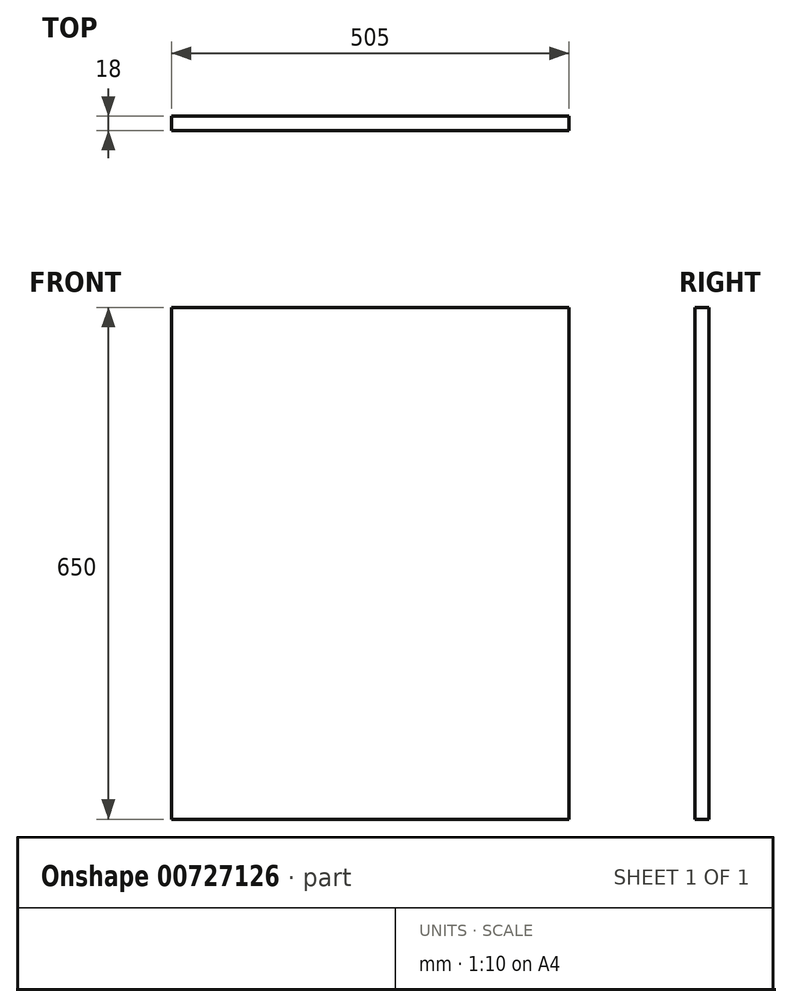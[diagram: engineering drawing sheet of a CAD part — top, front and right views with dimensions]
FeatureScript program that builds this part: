
annotation { "Feature Type Name" : "Feature", "Feature Type Description" : "" }
export const myFeature = defineFeature(function(context is Context, id is Id, definition is map)
    precondition{}
    {
        {
            var Q0;
            Q0=qCreatedBy(makeId("Front.planeOp"),FACE);
            var sketch = newSketch(context, id + "F0", { "sketchPlane" : qUnion([Q0])});
            skLineSegment(sketch, "E0.bottom", {"start": v(0, 0) * mm, "end": v(505, 0) * mm});
            skLineSegment(sketch, "E0.top", {"start": v(0, 650) * mm, "end": v(505, 650) * mm});
            skLineSegment(sketch, "E0.left", {"start": v(0, 0) * mm, "end": v(0, 650) * mm});
            skLineSegment(sketch, "E0.right", {"start": v(505, 0) * mm, "end": v(505, 650) * mm});
            skSolve(sketch);
        }
        {
            var Q0;
            Q0 = qSketchRegion(id + "F0", true);
            extrude(context, id + "F1", {"entities" : qUnion([Q0]), "depth" : 18 * mm, "offsetDistance" : 25 * mm});
        }
    });
